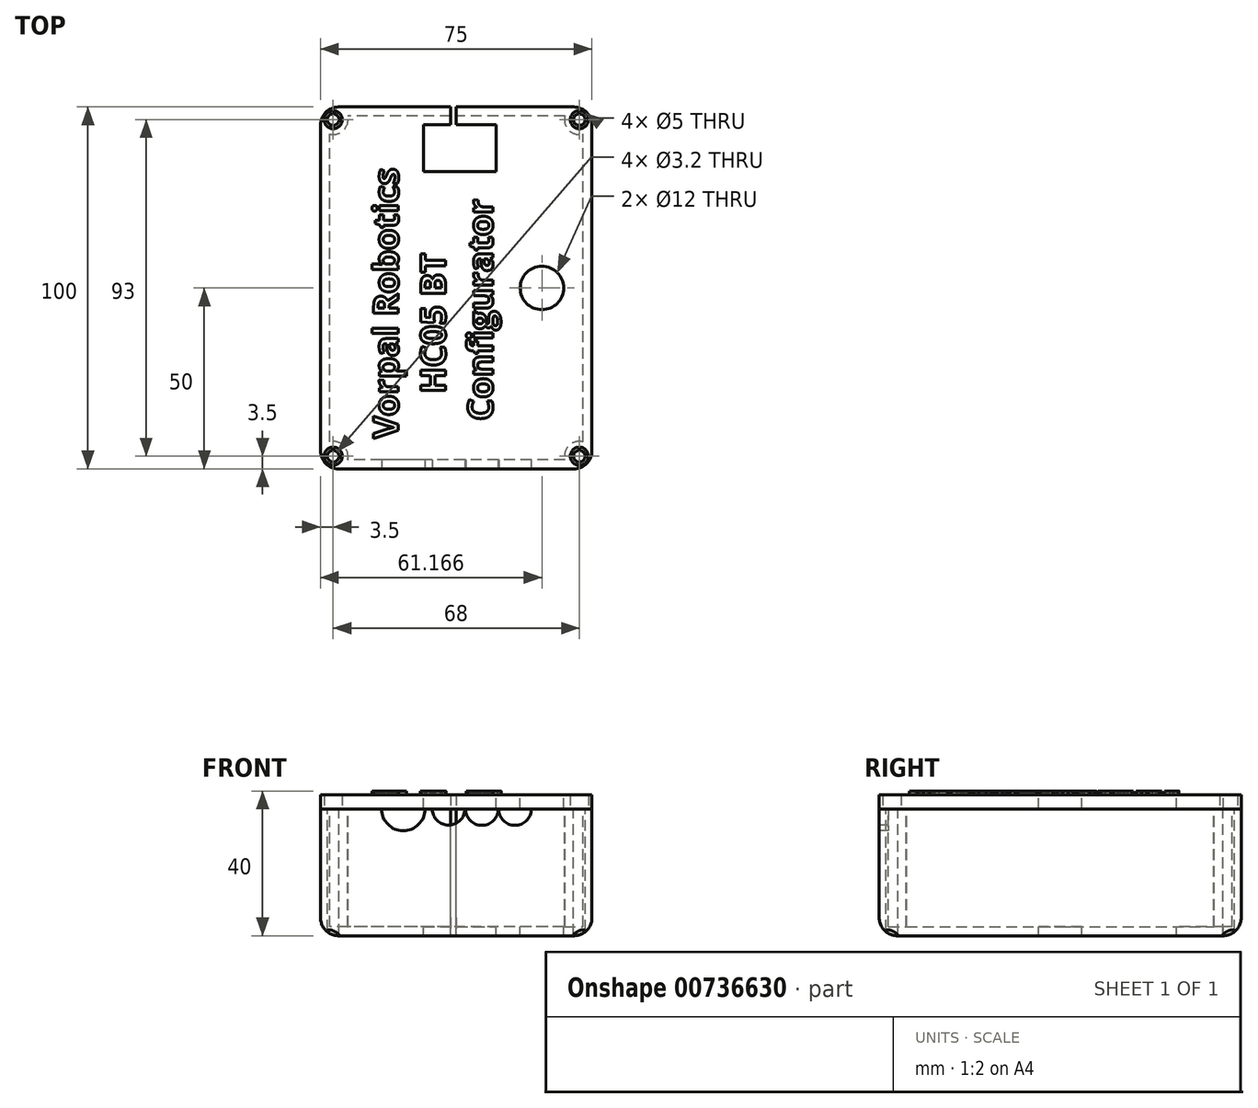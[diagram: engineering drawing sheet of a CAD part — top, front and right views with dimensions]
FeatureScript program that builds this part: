
annotation { "Feature Type Name" : "Feature", "Feature Type Description" : "" }
export const myFeature = defineFeature(function(context is Context, id is Id, definition is map)
    precondition{}
    {
        {
            var Q0;
            Q0=qCreatedBy(makeId("Top.planeOp"),FACE);
            var sketch = newSketch(context, id + "F0", { "sketchPlane" : qUnion([Q0])});
            skLineSegment(sketch, "E0.bottom", {"start": v(37.5, -50) * mm, "end": v(-37.5, -50) * mm});
            skLineSegment(sketch, "E0.top", {"start": v(37.5, 50) * mm, "end": v(-37.5, 50) * mm});
            skLineSegment(sketch, "E0.left", {"start": v(37.5, -50) * mm, "end": v(37.5, 50) * mm});
            skLineSegment(sketch, "E0.right", {"start": v(-37.5, -50) * mm, "end": v(-37.5, 50) * mm});
            skPoint(sketch, "E0.middle", {"position": v(0, 0) * mm});
            skLineSegment(sketch, "E1.bottom", {"start": v(34, -46.5) * mm, "end": v(-34, -46.5) * mm, "construction": true});
            skLineSegment(sketch, "E1.top", {"start": v(34, 46.5) * mm, "end": v(-34, 46.5) * mm, "construction": true});
            skLineSegment(sketch, "E1.left", {"start": v(34, -46.5) * mm, "end": v(34, 46.5) * mm, "construction": true});
            skLineSegment(sketch, "E1.right", {"start": v(-34, -46.5) * mm, "end": v(-34, 46.5) * mm, "construction": true});
            skCircle(sketch, "E2", {"center": v(-34, 46.5) * mm, "radius": 2.5 * mm});
            skCircle(sketch, "E3", {"center": v(34, 46.5) * mm, "radius": 2.5 * mm});
            skCircle(sketch, "E4", {"center": v(-34, -46.5) * mm, "radius": 2.5 * mm});
            skCircle(sketch, "E5", {"center": v(34, -46.5) * mm, "radius": 2.5 * mm});
            skCircle(sketch, "E6", {"center": v(-34, 46.5) * mm, "radius": 1.6 * mm});
            skCircle(sketch, "E7", {"center": v(34, 46.5) * mm, "radius": 1.6 * mm});
            skCircle(sketch, "E8", {"center": v(34, -46.5) * mm, "radius": 1.6 * mm});
            skCircle(sketch, "E9", {"center": v(-34, -46.5) * mm, "radius": 1.6 * mm});
            skSolve(sketch);
        }
        {
            var Q0;
            Q0 = qSketchRegion(id + "F0", true);
            var Q1;
            Q1=makeQuery(id+"F0.imprint","IMPRINT",FACE,{"disambiguationData":[TD([[makeQuery(id+"F0.imprint","IMPRINT",EDGE,{"derivedFrom":sQuery(id+"F0.wireOp",EDGE,"E2")}),1.0]])]});
            var Q2;
            Q2=makeQuery(id+"F0.imprint","IMPRINT",FACE,{"disambiguationData":[TD([[makeQuery(id+"F0.imprint","IMPRINT",EDGE,{"derivedFrom":sQuery(id+"F0.wireOp",EDGE,"E3")}),1.0]])]});
            var Q3;
            Q3=makeQuery(id+"F0.imprint","IMPRINT",FACE,{"disambiguationData":[TD([[makeQuery(id+"F0.imprint","IMPRINT",EDGE,{"derivedFrom":sQuery(id+"F0.wireOp",EDGE,"E4")}),1.0]])]});
            var Q4;
            Q4=makeQuery(id+"F0.imprint","IMPRINT",FACE,{"disambiguationData":[TD([[makeQuery(id+"F0.imprint","IMPRINT",EDGE,{"derivedFrom":sQuery(id+"F0.wireOp",EDGE,"E5")}),1.0]])]});
            extrude(context, id + "F1", {"entities" : qUnion([Q0, Q1, Q2, Q3, Q4]), "oppositeDirection" : true, "depth" : 35 * mm, "offsetDistance" : 25 * mm});
        }
        {
            var Q0;
            Q0=makeQuery(id+"F1.opExtrude","CAP_FACE",FACE,{"disambiguationData":[OSD([sQuery(id+"F0.wireOp",EDGE,"E0.bottom"),sQuery(id+"F0.wireOp",EDGE,"E0.top"),sQuery(id+"F0.wireOp",EDGE,"E0.left"),sQuery(id+"F0.wireOp",EDGE,"E0.right"),sQuery(id+"F0.wireOp",EDGE,"E6"),sQuery(id+"F0.wireOp",EDGE,"E7"),sQuery(id+"F0.wireOp",EDGE,"E8"),sQuery(id+"F0.wireOp",EDGE,"E9")])],"isStart":true});
            shell(context, id + "F2", {"entities" : qUnion([Q0]), "thickness" : 2.5 * mm});
        }
        {
            var Q0;
            Q0=makeQuery(id+"F1.opExtrude","SWEPT_EDGE",EDGE,{"disambiguationData":[OSD([sQuery(id+"F0.wireOp",EDGE,"E0.bottom"),sQuery(id+"F0.wireOp",EDGE,"E0.right")])]});
            var Q1;
            Q1=makeQuery(id+"F1.opExtrude","SWEPT_EDGE",EDGE,{"disambiguationData":[OSD([sQuery(id+"F0.wireOp",EDGE,"E0.bottom"),sQuery(id+"F0.wireOp",EDGE,"E0.left")])]});
            var Q2;
            Q2=makeQuery(id+"F1.opExtrude","SWEPT_EDGE",EDGE,{"disambiguationData":[OSD([sQuery(id+"F0.wireOp",EDGE,"E0.top"),sQuery(id+"F0.wireOp",EDGE,"E0.left")])]});
            var Q3;
            Q3=makeQuery(id+"F1.opExtrude","SWEPT_EDGE",EDGE,{"disambiguationData":[OSD([sQuery(id+"F0.wireOp",EDGE,"E0.top"),sQuery(id+"F0.wireOp",EDGE,"E0.right")])]});
            var Q4;
            Q4=makeQuery(id+"F1.opExtrude","CAP_EDGE",EDGE,{"disambiguationData":[OSD([sQuery(id+"F0.wireOp",EDGE,"E0.top")])],"isStart":false});
            var Q5;
            Q5=makeQuery(id+"F1.opExtrude","CAP_EDGE",EDGE,{"disambiguationData":[OSD([sQuery(id+"F0.wireOp",EDGE,"E0.right")])],"isStart":false});
            var Q6;
            Q6=makeQuery(id+"F1.opExtrude","CAP_EDGE",EDGE,{"disambiguationData":[OSD([sQuery(id+"F0.wireOp",EDGE,"E0.bottom")])],"isStart":false});
            var Q7;
            Q7=makeQuery(id+"F1.opExtrude","CAP_EDGE",EDGE,{"disambiguationData":[OSD([sQuery(id+"F0.wireOp",EDGE,"E0.left")])],"isStart":false});
            fillet(context, id + "F3", {"entities" : qUnion([Q0, Q1, Q2, Q3, Q4, Q5, Q6, Q7]), "radius" : 5 * mm, "allowEdgeOverflow" : false});
        }
        {
            var Q0;
            Q0=makeQuery(id+"F1.opExtrude","SWEPT_FACE",FACE,{"disambiguationData":[OSD([sQuery(id+"F0.wireOp",EDGE,"E0.bottom")])]});
            var sketch = newSketch(context, id + "F4", { "sketchPlane" : qUnion([Q0])});
            skCircle(sketch, "E10", {"center": v(-14.63, 0) * mm, "radius": 6 * mm});
            skCircle(sketch, "E11", {"center": v(-2.11, 0.07) * mm, "radius": 4.5 * mm});
            skCircle(sketch, "E12", {"center": v(7.1, 0) * mm, "radius": 4.5 * mm});
            skCircle(sketch, "E13", {"center": v(16.23, 0) * mm, "radius": 4.5 * mm});
            skSolve(sketch);
        }
        {
            var Q0;
            Q0 = qSketchRegion(id + "F4", true);
            extrude(context, id + "F5", {"entities" : qUnion([Q0]), "operationType" : NewBodyOperationType.REMOVE, "oppositeDirection" : true, "depth" : 25 * mm, "offsetDistance" : 25 * mm});
        }
        {
            var Q0;
            Q0 = qSketchRegion(id + "F0", true);
            extrude(context, id + "F6", {"entities" : qUnion([Q0]), "depth" : 4 * mm, "offsetDistance" : 25 * mm});
        }
        {
            var Q0;
            Q0=makeQuery(id+"F6.opExtrude","SWEPT_EDGE",EDGE,{"disambiguationData":[OSD([sQuery(id+"F0.wireOp",EDGE,"E0.bottom"),sQuery(id+"F0.wireOp",EDGE,"E0.right")])]});
            var Q1;
            Q1=makeQuery(id+"F6.opExtrude","SWEPT_EDGE",EDGE,{"disambiguationData":[OSD([sQuery(id+"F0.wireOp",EDGE,"E0.bottom"),sQuery(id+"F0.wireOp",EDGE,"E0.left")])]});
            var Q2;
            Q2=makeQuery(id+"F6.opExtrude","SWEPT_EDGE",EDGE,{"disambiguationData":[OSD([sQuery(id+"F0.wireOp",EDGE,"E0.top"),sQuery(id+"F0.wireOp",EDGE,"E0.left")])]});
            var Q3;
            Q3=makeQuery(id+"F6.opExtrude","SWEPT_EDGE",EDGE,{"disambiguationData":[OSD([sQuery(id+"F0.wireOp",EDGE,"E0.top"),sQuery(id+"F0.wireOp",EDGE,"E0.right")])]});
            fillet(context, id + "F7", {"entities" : qUnion([Q0, Q1, Q2, Q3]), "radius" : 5 * mm, "tangentPropagation" : true, "allowEdgeOverflow" : false});
        }
        {
            var Q0;
            Q0=makeQuery(id+"F6.opExtrude","CAP_FACE",FACE,{"disambiguationData":[OSD([sQuery(id+"F0.wireOp",EDGE,"E0.bottom"),sQuery(id+"F0.wireOp",EDGE,"E0.top"),sQuery(id+"F0.wireOp",EDGE,"E0.left"),sQuery(id+"F0.wireOp",EDGE,"E0.right"),sQuery(id+"F0.wireOp",EDGE,"E2"),sQuery(id+"F0.wireOp",EDGE,"E3"),sQuery(id+"F0.wireOp",EDGE,"E4"),sQuery(id+"F0.wireOp",EDGE,"E5")])],"isStart":false});
            var sketch = newSketch(context, id + "F8", { "sketchPlane" : qUnion([Q0])});
            skLineSegment(sketch, "E14.bottom", {"start": v(-8.99, 45.1) * mm, "end": v(-1.5, 45.1) * mm});
            skLineSegment(sketch, "E14.top", {"start": v(-8.99, 32.1) * mm, "end": v(11.01, 32.1) * mm});
            skLineSegment(sketch, "E14.left", {"start": v(-8.99, 45.1) * mm, "end": v(-8.99, 32.1) * mm});
            skLineSegment(sketch, "E14.right", {"start": v(11.01, 45.1) * mm, "end": v(11.01, 32.1) * mm});
            skLineSegment(sketch, "E15.bottom", {"start": v(-1.5, 53.63) * mm, "end": v(0, 53.63) * mm});
            skLineSegment(sketch, "E15.left", {"start": v(-1.5, 53.63) * mm, "end": v(-1.5, 45.1) * mm});
            skLineSegment(sketch, "E15.right", {"start": v(0, 53.63) * mm, "end": v(0, 45.1) * mm});
            skLineSegment(sketch, "E16.trimOffspring", {"start": v(0, 45.1) * mm, "end": v(11.01, 45.1) * mm});
            skCircle(sketch, "E17", {"center": v(23.67, 0) * mm, "radius": 6 * mm});
            skPoint(sketch, "E17.centerSnap0", {"position": v(37.5, 0) * mm});
            skSolve(sketch);
        }
        {
            var Q0;
            Q0 = qSketchRegion(id + "F8", true);
            extrude(context, id + "F9", {"entities" : qUnion([Q0]), "operationType" : NewBodyOperationType.REMOVE, "endBound" : BoundingType.THROUGH_ALL, "oppositeDirection" : true, "depth" : 25 * mm, "offsetDistance" : 25 * mm});
        }
        {
            var Q0;
            Q0=makeQuery(id+"F6.opExtrude","CAP_FACE",FACE,{"disambiguationData":[OSD([sQuery(id+"F0.wireOp",EDGE,"E0.bottom"),sQuery(id+"F0.wireOp",EDGE,"E0.top"),sQuery(id+"F0.wireOp",EDGE,"E0.left"),sQuery(id+"F0.wireOp",EDGE,"E0.right"),sQuery(id+"F0.wireOp",EDGE,"E2"),sQuery(id+"F0.wireOp",EDGE,"E3"),sQuery(id+"F0.wireOp",EDGE,"E4"),sQuery(id+"F0.wireOp",EDGE,"E5")])],"isStart":false});
            var sketch = newSketch(context, id + "F10", { "sketchPlane" : qUnion([Q0])});
            skText(sketch, "E18", { "text": "Vorpal Robotics\n     HC05 BT\n  Configurator", "fontName": "OpenSans-Bold.ttf"});
            const initialGuessF10  = {"E18": [-0.01598, -0.04165, 0, 1, 0.0069]};
            skSetInitialGuess(sketch, initialGuessF10);
            skSolve(sketch);
        }
        {
            var Q0;
            Q0 = qSketchRegion(id + "F10", true);
            extrude(context, id + "F11", {"entities" : qUnion([Q0]), "operationType" : NewBodyOperationType.ADD, "depth" : 1 * mm, "offsetDistance" : 25 * mm});
        }
    });
